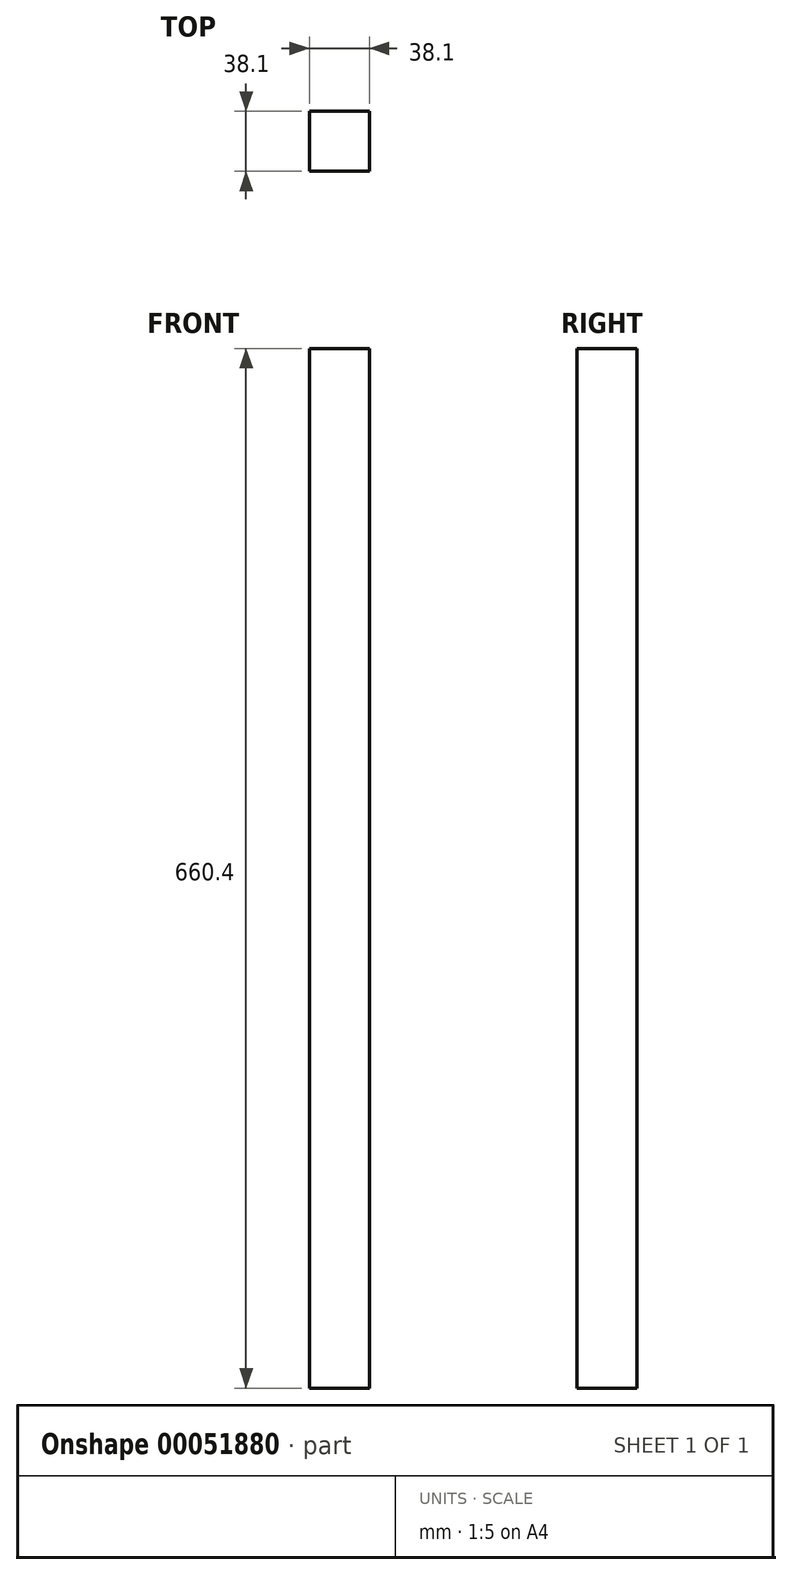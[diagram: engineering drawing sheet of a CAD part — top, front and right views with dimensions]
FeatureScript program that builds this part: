
annotation { "Feature Type Name" : "Feature", "Feature Type Description" : "" }
export const myFeature = defineFeature(function(context is Context, id is Id, definition is map)
    precondition{}
    {
        {
            var Q0;
            Q0=qCreatedBy(makeId("Top.planeOp"),FACE);
            var sketch = newSketch(context, id + "F0", { "sketchPlane" : qUnion([Q0])});
            skLineSegment(sketch, "E0.bottom", {"start": v(-19.05, 19.05) * mm, "end": v(19.05, 19.05) * mm});
            skLineSegment(sketch, "E0.top", {"start": v(-19.05, -19.05) * mm, "end": v(19.05, -19.05) * mm});
            skLineSegment(sketch, "E0.left", {"start": v(-19.05, 19.05) * mm, "end": v(-19.05, -19.05) * mm});
            skLineSegment(sketch, "E0.right", {"start": v(19.05, 19.05) * mm, "end": v(19.05, -19.05) * mm});
            skSolve(sketch);
        }
        {
            var Q0;
            Q0 = qSketchRegion(id + "F0", true);
            extrude(context, id + "F1", {"entities" : qUnion([Q0]), "depth" : 660.4 * mm});
        }
    });
